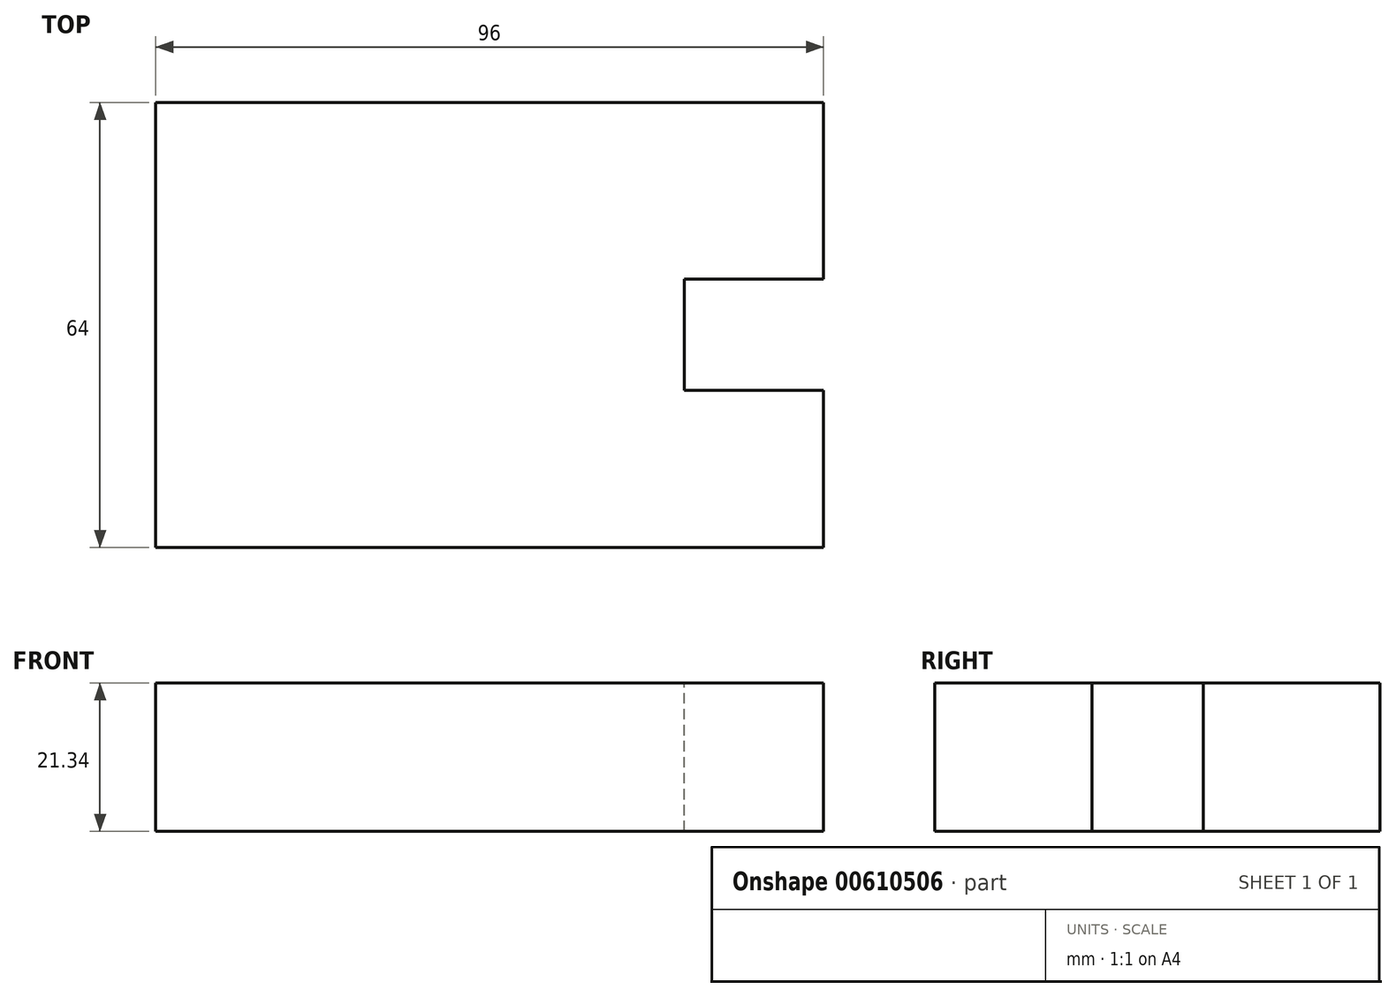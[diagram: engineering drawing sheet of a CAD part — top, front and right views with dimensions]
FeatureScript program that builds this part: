
annotation { "Feature Type Name" : "Feature", "Feature Type Description" : "" }
export const myFeature = defineFeature(function(context is Context, id is Id, definition is map)
    precondition{}
    {
        {
            var Q0;
            Q0=qCreatedBy(makeId("Top.planeOp"),FACE);
            var sketch = newSketch(context, id + "F0", { "sketchPlane" : qUnion([Q0])});
            skLineSegment(sketch, "E0.bottom", {"start": v(-41.5, 41.42) * mm, "end": v(54.5, 41.42) * mm});
            skLineSegment(sketch, "E0.top", {"start": v(-41.5, -22.58) * mm, "end": v(54.5, -22.58) * mm});
            skLineSegment(sketch, "E0.left", {"start": v(-41.5, 41.42) * mm, "end": v(-41.5, -22.58) * mm});
            skLineSegment(sketch, "E0.right", {"start": v(54.5, 41.42) * mm, "end": v(54.5, -22.58) * mm});
            skSolve(sketch);
        }
        {
            var Q0;
            Q0 = qSketchRegion(id + "F0", true);
            extrude(context, id + "F1", {"entities" : qUnion([Q0]), "depth" : 21.34 * mm, "offsetDistance" : 25.4 * mm});
        }
        {
            var Q0;
            Q0=makeQuery(id+"F1.opExtrude","CAP_FACE",FACE,{"disambiguationData":[OSD([sQuery(id+"F0.wireOp",EDGE,"E0.bottom"),sQuery(id+"F0.wireOp",EDGE,"E0.top"),sQuery(id+"F0.wireOp",EDGE,"E0.left"),sQuery(id+"F0.wireOp",EDGE,"E0.right")])],"isStart":false});
            var sketch = newSketch(context, id + "F2", { "sketchPlane" : qUnion([Q0])});
            skLineSegment(sketch, "E1.bottom", {"start": v(34.5, 16) * mm, "end": v(54.5, 16) * mm});
            skLineSegment(sketch, "E1.top", {"start": v(34.5, 0) * mm, "end": v(54.5, 0) * mm});
            skLineSegment(sketch, "E1.left", {"start": v(34.5, 16) * mm, "end": v(34.5, 0) * mm});
            skLineSegment(sketch, "E1.right", {"start": v(54.5, 16) * mm, "end": v(54.5, 0) * mm});
            skArc(sketch, "E2", {"start": v(34.5, 16) * mm, "mid": v(26.5, 8) * mm, "end": v(34.5, 0) * mm});
            skSolve(sketch);
        }
        {
            var Q0;
            Q0=makeQuery(id+"F2.imprint","IMPRINT",FACE,{"disambiguationData":[TD([[makeQuery(id+"F2.imprint","IMPRINT",EDGE,{"derivedFrom":sQuery(id+"F2.wireOp",EDGE,"E1.bottom")}),-1.0]])]});
            extrude(context, id + "F3", {"entities" : qUnion([Q0]), "operationType" : NewBodyOperationType.REMOVE, "oppositeDirection" : true, "depth" : 118.1 * mm, "offsetDistance" : 25.4 * mm});
        }
    });
